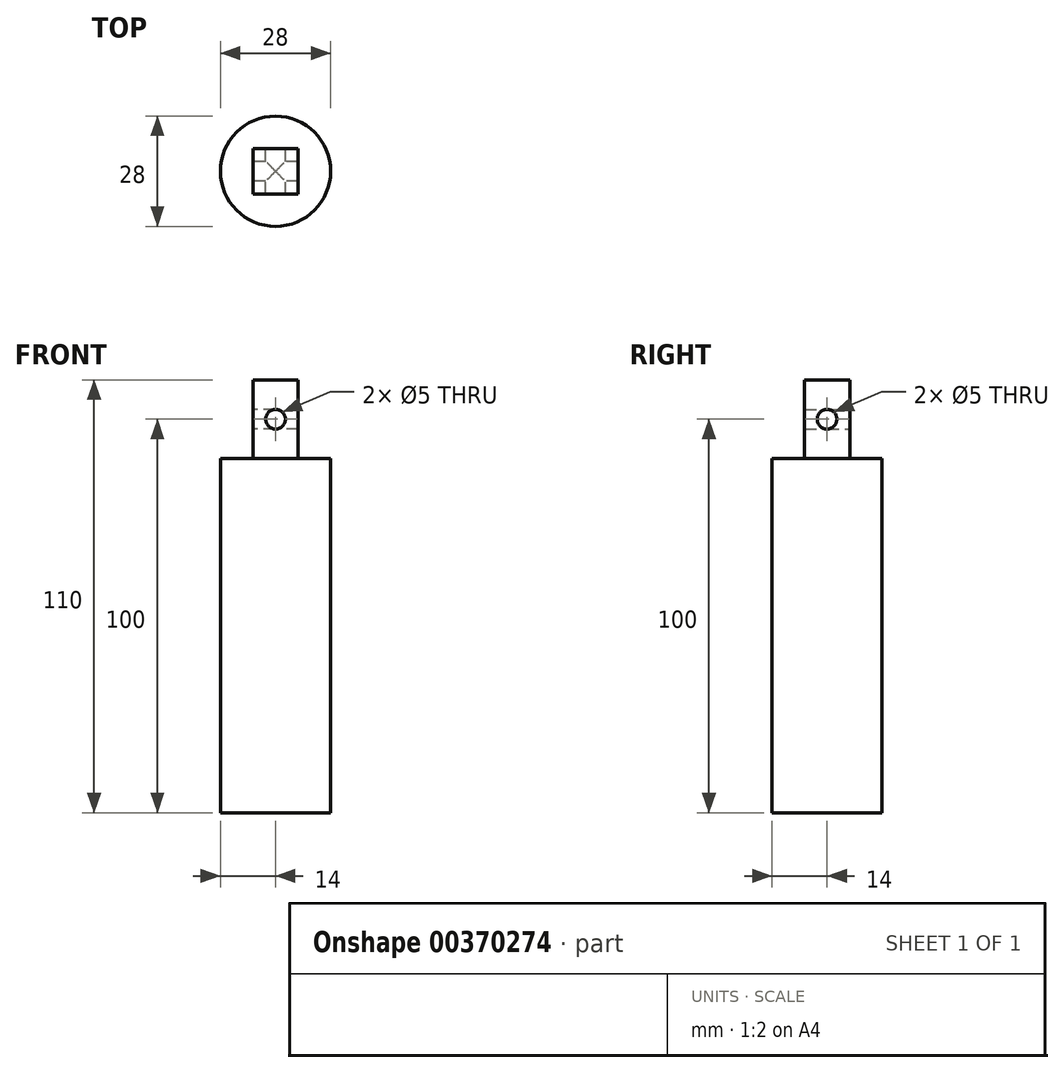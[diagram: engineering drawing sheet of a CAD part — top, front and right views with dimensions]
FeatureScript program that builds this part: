
annotation { "Feature Type Name" : "Feature", "Feature Type Description" : "" }
export const myFeature = defineFeature(function(context is Context, id is Id, definition is map)
    precondition{}
    {
        {
            var Q0;
            Q0=qCreatedBy(makeId("Top.planeOp"),FACE);
            var sketch = newSketch(context, id + "F0", { "sketchPlane" : qUnion([Q0])});
            skCircle(sketch, "E0", {"center": v(0, 0) * mm, "radius": 14 * mm});
            skLineSegment(sketch, "E1.bottom", {"start": v(5.75, 5.75) * mm, "end": v(-5.75, 5.75) * mm});
            skLineSegment(sketch, "E1.top", {"start": v(5.75, -5.75) * mm, "end": v(-5.75, -5.75) * mm});
            skLineSegment(sketch, "E1.left", {"start": v(5.75, 5.75) * mm, "end": v(5.75, -5.75) * mm});
            skLineSegment(sketch, "E1.right", {"start": v(-5.75, 5.75) * mm, "end": v(-5.75, -5.75) * mm});
            skSolve(sketch);
        }
        {
            var Q0;
            Q0=makeQuery(id+"F0.imprint","IMPRINT",FACE,{"disambiguationData":[TD([[makeQuery(id+"F0.imprint","IMPRINT",EDGE,{"derivedFrom":sQuery(id+"F0.wireOp",EDGE,"E1.bottom")}),1.0]])]});
            extrude(context, id + "F1", {"entities" : qUnion([Q0]), "depth" : 20 * mm});
        }
        {
            var Q0;
            Q0=makeQuery(id+"F0.imprint","IMPRINT",FACE,{"disambiguationData":[TD([[makeQuery(id+"F0.imprint","IMPRINT",EDGE,{"derivedFrom":sQuery(id+"F0.wireOp",EDGE,"E0")}),1.0]])]});
            var Q1;
            Q1=makeQuery(id+"F0.imprint","IMPRINT",FACE,{"disambiguationData":[TD([[makeQuery(id+"F0.imprint","IMPRINT",EDGE,{"derivedFrom":sQuery(id+"F0.wireOp",EDGE,"E1.bottom")}),1.0]])]});
            extrude(context, id + "F2", {"entities" : qUnion([Q0, Q1]), "operationType" : NewBodyOperationType.ADD, "oppositeDirection" : true, "depth" : 90 * mm});
        }
        {
            var Q0;
            Q0=makeQuery(id+"F1.opExtrude","SWEPT_FACE",FACE,{"disambiguationData":[OSD([sQuery(id+"F0.wireOp",EDGE,"E1.bottom")])]});
            var sketch = newSketch(context, id + "F3", { "sketchPlane" : qUnion([Q0])});
            skCircle(sketch, "E2", {"center": v(0, 10) * mm, "radius": 2.5 * mm});
            skSolve(sketch);
        }
        {
            var Q0;
            Q0=makeQuery(id+"F3.imprint","IMPRINT",FACE,{"disambiguationData":[TD([[makeQuery(id+"F3.imprint","IMPRINT",EDGE,{"derivedFrom":sQuery(id+"F3.wireOp",EDGE,"E2")}),1.0]])]});
            extrude(context, id + "F4", {"entities" : qUnion([Q0]), "operationType" : NewBodyOperationType.REMOVE, "endBound" : BoundingType.THROUGH_ALL, "oppositeDirection" : true, "depth" : 25 * mm});
        }
        {
            var Q0;
            Q0=qCreatedBy(makeId("Front.planeOp"),FACE);
            var sketch = newSketch(context, id + "F5", { "sketchPlane" : qUnion([Q0])});
            skLineSegment(sketch, "E3", {"start": v(14, 0) * mm, "end": v(14, -90) * mm});
            skLineSegment(sketch, "E4", {"start": v(-14, -90) * mm, "end": v(-14, 0) * mm});
            skLineSegment(sketch, "E5", {"start": v(14, -45) * mm, "end": v(46.06, -45) * mm, "construction": true});
            skSolve(sketch);
        }
        {
            var Q0;
            Q0=sQuery(id+"F5.wireOp",EDGE,"E5");
            cPlane(context, id + "F6", {"entities" : qUnion([Q0]), "cplaneType" : CPlaneType.LINE_ANGLE, "offset" : 25 * mm, "angle" : 90 * degree, "width" : 150 * mm, "height" : 150 * mm});
        }
        {
            var Q0;
            Q0=makeQuery(id+"FeaQ6zaSpsTjrf2_1.1.F1.opExtrude","CAP_FACE",FACE,{"disambiguationData":[OSD([sQuery(id+"F0.wireOp",EDGE,"E1.bottom"),sQuery(id+"F0.wireOp",EDGE,"E1.top"),sQuery(id+"F0.wireOp",EDGE,"E1.left"),sQuery(id+"F0.wireOp",EDGE,"E1.right")])],"isStart":false});
            var sketch = newSketch(context, id + "F7", { "sketchPlane" : qUnion([Q0])});
            skSolve(sketch);
        }
        {
            var Q0;
            Q0=makeQuery(id+"F1.opExtrude","SWEPT_FACE",FACE,{"disambiguationData":[OSD([sQuery(id+"F0.wireOp",EDGE,"E1.right")])]});
            var sketch = newSketch(context, id + "F8", { "sketchPlane" : qUnion([Q0])});
            skPoint(sketch, "E6.endSnap0", {"position": v(0, 20) * mm});
            skCircle(sketch, "E7", {"center": v(0, 10) * mm, "radius": 2.5 * mm});
            skCircle(sketch, "E8", {"center": v(0, -100.2) * mm, "radius": 2.5 * mm});
            skSolve(sketch);
        }
        {
            var Q0;
            Q0=makeQuery(id+"F8.imprint","IMPRINT",FACE,{"disambiguationData":[TD([[makeQuery(id+"F8.imprint","IMPRINT",EDGE,{"derivedFrom":sQuery(id+"F8.wireOp",EDGE,"E7")}),1.0]])]});
            var Q1;
            Q1=makeQuery(id+"F8.imprint","IMPRINT",FACE,{"disambiguationData":[TD([[makeQuery(id+"F8.imprint","IMPRINT",EDGE,{"derivedFrom":sQuery(id+"F8.wireOp",EDGE,"E8")}),1.0]])]});
            extrude(context, id + "F9", {"entities" : qUnion([Q0, Q1]), "operationType" : NewBodyOperationType.REMOVE, "oppositeDirection" : true, "depth" : 25 * mm});
        }
    });
